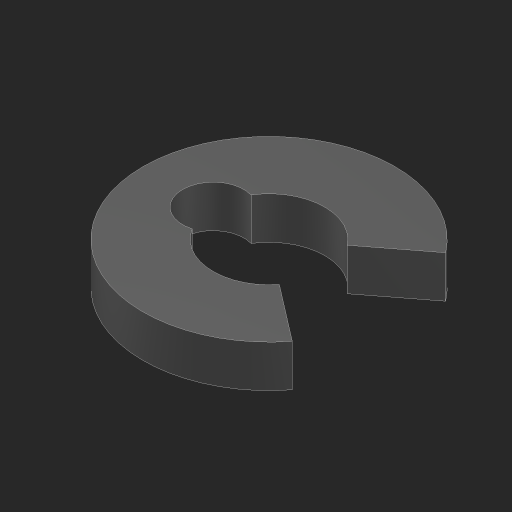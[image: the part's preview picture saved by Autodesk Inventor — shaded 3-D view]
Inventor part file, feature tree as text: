
AUTODESK INVENTOR PART (.ipt)
format: ipt  version: 2023 (Build 270158000, 158)  size: 108,544 bytes
history: native  units: in
note: dims shown in document units (in); Inventor stores cm internally (conversion verified against a paired STEP export)
features: other x4, extrude x1, sketch x1
ambient origin geometry x8: Origin, YZ Plane, XZ Plane, XY Plane, X Axis, Y Axis, Z Axis, Center Point
bodies: Solid1 (feature_tree)
feature tree (6):
  other  "Table"
  other  "Nspacer Click On x .0625"
  other  "Nspacer Click On x .1250"
  other  "Nspacer Click On x .2500"
  extrude  "Extrusion1"  Depth=0.166in
  sketch  "Sketch1"  dims[d0=0.375in d1=0.166in d2=0.091in d3=75.0deg d5=0.0in]
